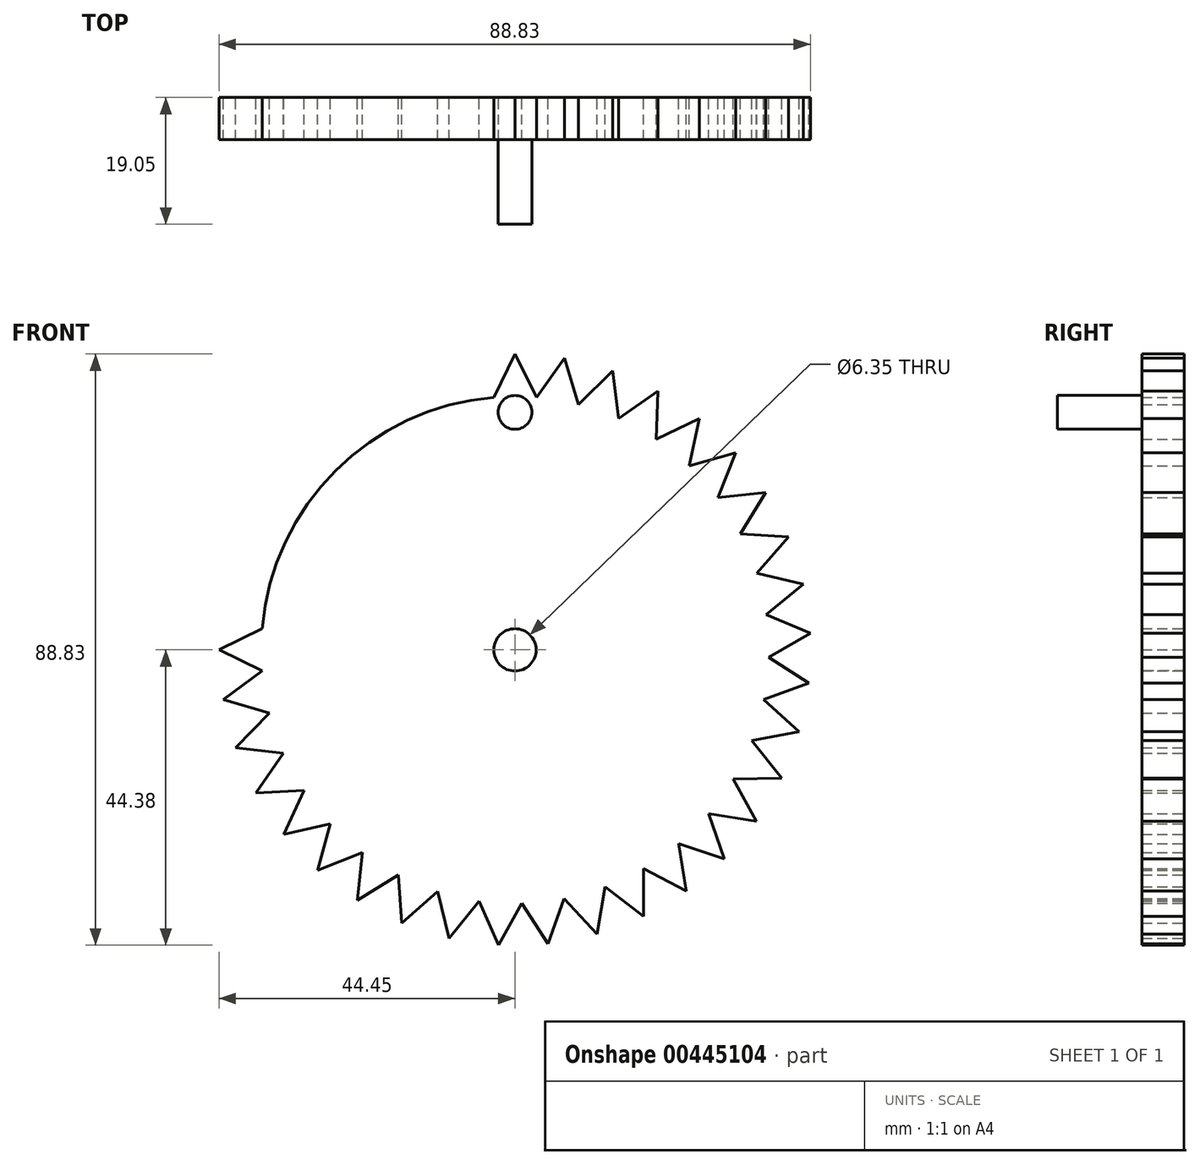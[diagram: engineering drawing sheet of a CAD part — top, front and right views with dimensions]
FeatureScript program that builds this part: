
annotation { "Feature Type Name" : "Feature", "Feature Type Description" : "" }
export const myFeature = defineFeature(function(context is Context, id is Id, definition is map)
    precondition{}
    {
        {
            var Q0;
            Q0=qCreatedBy(makeId("Front.planeOp"),FACE);
            var sketch = newSketch(context, id + "F0", { "sketchPlane" : qUnion([Q0])});
            skCircle(sketch, "E0", {"center": v(0, 0) * mm, "radius": 38.1 * mm});
            skPoint(sketch, "E1", {"position": v(0, 38.1) * mm});
            skPoint(sketch, "E2.1.0", {"position": v(6.38, 37.56) * mm});
            skPoint(sketch, "E2.2.0", {"position": v(12.58, 35.96) * mm});
            skPoint(sketch, "E2.3.0", {"position": v(18.43, 33.35) * mm});
            skPoint(sketch, "E2.4.0", {"position": v(23.75, 29.79) * mm});
            skPoint(sketch, "E2.5.0", {"position": v(28.4, 25.39) * mm});
            skPoint(sketch, "E2.6.0", {"position": v(32.26, 20.27) * mm});
            skPoint(sketch, "E2.7.0", {"position": v(35.2, 14.58) * mm});
            skPoint(sketch, "E2.8.0", {"position": v(37.14, 8.48) * mm});
            skPoint(sketch, "E2.9.0", {"position": v(38.04, 2.14) * mm});
            skPoint(sketch, "E2.10.0", {"position": v(37.86, -4.27) * mm});
            skPoint(sketch, "E2.11.0", {"position": v(36.61, -10.55) * mm});
            skPoint(sketch, "E2.12.0", {"position": v(34.33, -16.53) * mm});
            skPoint(sketch, "E2.13.0", {"position": v(31.07, -22.05) * mm});
            skPoint(sketch, "E2.14.0", {"position": v(26.94, -26.94) * mm});
            skPoint(sketch, "E2.15.0", {"position": v(22.05, -31.07) * mm});
            skPoint(sketch, "E2.16.0", {"position": v(16.53, -34.33) * mm});
            skPoint(sketch, "E2.17.0", {"position": v(10.55, -36.61) * mm});
            skPoint(sketch, "E2.18.0", {"position": v(4.27, -37.86) * mm});
            skPoint(sketch, "E2.19.0", {"position": v(-2.14, -38.04) * mm});
            skPoint(sketch, "E2.20.0", {"position": v(-8.48, -37.14) * mm});
            skPoint(sketch, "E2.21.0", {"position": v(-14.58, -35.2) * mm});
            skPoint(sketch, "E2.22.0", {"position": v(-20.27, -32.26) * mm});
            skPoint(sketch, "E2.23.0", {"position": v(-25.39, -28.4) * mm});
            skPoint(sketch, "E2.24.0", {"position": v(-29.79, -23.75) * mm});
            skPoint(sketch, "E2.25.0", {"position": v(-33.35, -18.43) * mm});
            skPoint(sketch, "E2.26.0", {"position": v(-35.96, -12.58) * mm});
            skPoint(sketch, "E2.27.0", {"position": v(-37.56, -6.38) * mm});
            skLineSegment(sketch, "E2.anchor1", {"start": v(0, 0) * mm, "end": v(0, 38.1) * mm, "construction": true});
            skLineSegment(sketch, "E2.anchor2", {"start": v(0, 0) * mm, "end": v(-38.1, 0) * mm, "construction": true});
            skPoint(sketch, "E3.0.28.0", {"position": v(-38.1, 0) * mm});
            skPoint(sketch, "E4", {"position": v(-3.17, 37.97) * mm});
            skPoint(sketch, "E5.1.0", {"position": v(3.23, 37.96) * mm});
            skPoint(sketch, "E5.2.0", {"position": v(9.55, 36.88) * mm});
            skPoint(sketch, "E5.3.0", {"position": v(15.59, 34.76) * mm});
            skPoint(sketch, "E5.4.0", {"position": v(21.2, 31.66) * mm});
            skPoint(sketch, "E5.5.0", {"position": v(26.2, 27.67) * mm});
            skPoint(sketch, "E5.6.0", {"position": v(30.46, 22.89) * mm});
            skPoint(sketch, "E5.7.0", {"position": v(33.86, 17.46) * mm});
            skPoint(sketch, "E5.8.0", {"position": v(36.3, 11.54) * mm});
            skPoint(sketch, "E5.9.0", {"position": v(37.73, 5.3) * mm});
            skPoint(sketch, "E5.10.0", {"position": v(38.08, -1.1) * mm});
            skPoint(sketch, "E5.11.0", {"position": v(37.36, -7.46) * mm});
            skPoint(sketch, "E5.12.0", {"position": v(35.58, -13.62) * mm});
            skPoint(sketch, "E5.13.0", {"position": v(32.8, -19.38) * mm});
            skPoint(sketch, "E5.14.0", {"position": v(29.1, -24.6) * mm});
            skPoint(sketch, "E5.15.0", {"position": v(24.56, -29.13) * mm});
            skPoint(sketch, "E5.16.0", {"position": v(19.33, -32.83) * mm});
            skPoint(sketch, "E5.17.0", {"position": v(13.56, -35.6) * mm});
            skPoint(sketch, "E5.18.0", {"position": v(7.4, -37.37) * mm});
            skPoint(sketch, "E5.19.0", {"position": v(1.04, -38.09) * mm});
            skPoint(sketch, "E5.20.0", {"position": v(-5.36, -37.72) * mm});
            skPoint(sketch, "E5.21.0", {"position": v(-11.6, -36.3) * mm});
            skPoint(sketch, "E5.22.0", {"position": v(-17.51, -33.84) * mm});
            skPoint(sketch, "E5.23.0", {"position": v(-22.93, -30.42) * mm});
            skPoint(sketch, "E5.24.0", {"position": v(-27.7, -26.15) * mm});
            skPoint(sketch, "E5.25.0", {"position": v(-31.7, -21.14) * mm});
            skPoint(sketch, "E5.26.0", {"position": v(-34.79, -15.53) * mm});
            skPoint(sketch, "E5.27.0", {"position": v(-36.9, -9.49) * mm});
            skPoint(sketch, "E5.28.0", {"position": v(-37.97, -3.17) * mm});
            skLineSegment(sketch, "E5.anchor1", {"start": v(0, 0) * mm, "end": v(-3.17, 37.97) * mm, "construction": true});
            skLineSegment(sketch, "E5.anchor2", {"start": v(0, 0) * mm, "end": v(-37.97, -3.17) * mm, "construction": true});
            skLineSegment(sketch, "E6", {"start": v(6.38, 37.56) * mm, "end": v(0, 0) * mm});
            skLineSegment(sketch, "E7", {"start": v(12.58, 35.96) * mm, "end": v(0, 0) * mm});
            skLineSegment(sketch, "E8", {"start": v(18.43, 33.35) * mm, "end": v(0, 0) * mm});
            skLineSegment(sketch, "E9", {"start": v(23.75, 29.79) * mm, "end": v(0, 0) * mm});
            skLineSegment(sketch, "E10", {"start": v(28.4, 25.39) * mm, "end": v(0, 0) * mm});
            skLineSegment(sketch, "E11", {"start": v(32.26, 20.27) * mm, "end": v(0, 0) * mm});
            skLineSegment(sketch, "E12", {"start": v(35.2, 14.58) * mm, "end": v(0, 0) * mm});
            skLineSegment(sketch, "E13", {"start": v(37.14, 8.48) * mm, "end": v(0, 0) * mm});
            skLineSegment(sketch, "E14", {"start": v(38.04, 2.14) * mm, "end": v(0, 0) * mm});
            skLineSegment(sketch, "E15", {"start": v(37.86, -4.27) * mm, "end": v(0, 0) * mm});
            skLineSegment(sketch, "E16", {"start": v(36.61, -10.55) * mm, "end": v(0, 0) * mm});
            skLineSegment(sketch, "E17", {"start": v(34.33, -16.53) * mm, "end": v(0, 0) * mm});
            skLineSegment(sketch, "E18", {"start": v(31.07, -22.05) * mm, "end": v(0, 0) * mm});
            skLineSegment(sketch, "E19", {"start": v(26.94, -26.94) * mm, "end": v(0, 0) * mm});
            skLineSegment(sketch, "E20", {"start": v(22.05, -31.07) * mm, "end": v(0, 0) * mm});
            skLineSegment(sketch, "E21", {"start": v(16.53, -34.33) * mm, "end": v(0, 0) * mm});
            skLineSegment(sketch, "E22", {"start": v(10.55, -36.61) * mm, "end": v(0, 0) * mm});
            skLineSegment(sketch, "E23", {"start": v(4.27, -37.86) * mm, "end": v(0, 0) * mm});
            skLineSegment(sketch, "E24", {"start": v(-2.14, -38.04) * mm, "end": v(0, 0) * mm});
            skLineSegment(sketch, "E25", {"start": v(-8.48, -37.14) * mm, "end": v(0, 0) * mm});
            skLineSegment(sketch, "E26", {"start": v(-14.58, -35.2) * mm, "end": v(0, 0) * mm});
            skLineSegment(sketch, "E27", {"start": v(-20.27, -32.26) * mm, "end": v(0, 0) * mm});
            skLineSegment(sketch, "E28", {"start": v(-25.39, -28.4) * mm, "end": v(0, 0) * mm});
            skLineSegment(sketch, "E29", {"start": v(-29.79, -23.75) * mm, "end": v(0, 0) * mm});
            skLineSegment(sketch, "E30", {"start": v(-33.35, -18.43) * mm, "end": v(0, 0) * mm});
            skLineSegment(sketch, "E31", {"start": v(-35.96, -12.58) * mm, "end": v(0, 0) * mm});
            skLineSegment(sketch, "E32", {"start": v(-37.56, -6.38) * mm, "end": v(0, 0) * mm});
            skLineSegment(sketch, "E33", {"start": v(0, 38.1) * mm, "end": v(0, 44.45) * mm});
            skLineSegment(sketch, "E34", {"start": v(6.38, 37.56) * mm, "end": v(7.45, 43.82) * mm});
            skLineSegment(sketch, "E35", {"start": v(12.58, 35.96) * mm, "end": v(14.68, 41.96) * mm});
            skLineSegment(sketch, "E36", {"start": v(18.43, 33.35) * mm, "end": v(21.5, 38.9) * mm});
            skLineSegment(sketch, "E37", {"start": v(23.75, 29.79) * mm, "end": v(27.71, 34.75) * mm});
            skLineSegment(sketch, "E38", {"start": v(28.4, 25.39) * mm, "end": v(33.14, 29.62) * mm});
            skLineSegment(sketch, "E39", {"start": v(32.26, 20.27) * mm, "end": v(37.64, 23.65) * mm});
            skLineSegment(sketch, "E40", {"start": v(35.2, 14.58) * mm, "end": v(41.07, 17.01) * mm});
            skLineSegment(sketch, "E41", {"start": v(37.14, 8.48) * mm, "end": v(43.34, 9.9) * mm});
            skLineSegment(sketch, "E42", {"start": v(38.04, 2.14) * mm, "end": v(44.38, 2.5) * mm});
            skLineSegment(sketch, "E43", {"start": v(37.86, -4.27) * mm, "end": v(44.17, -4.98) * mm});
            skLineSegment(sketch, "E44", {"start": v(36.61, -10.55) * mm, "end": v(42.71, -12.3) * mm});
            skLineSegment(sketch, "E45", {"start": v(34.33, -16.53) * mm, "end": v(40.05, -19.29) * mm});
            skLineSegment(sketch, "E46", {"start": v(31.07, -22.05) * mm, "end": v(36.25, -25.72) * mm});
            skLineSegment(sketch, "E47", {"start": v(26.94, -26.94) * mm, "end": v(31.43, -31.43) * mm});
            skLineSegment(sketch, "E48", {"start": v(22.05, -31.07) * mm, "end": v(25.72, -36.25) * mm});
            skLineSegment(sketch, "E49", {"start": v(16.53, -34.33) * mm, "end": v(19.29, -40.05) * mm});
            skLineSegment(sketch, "E50", {"start": v(10.55, -36.61) * mm, "end": v(12.3, -42.71) * mm});
            skLineSegment(sketch, "E51", {"start": v(4.27, -37.86) * mm, "end": v(4.98, -44.17) * mm});
            skLineSegment(sketch, "E52", {"start": v(-8.48, -37.14) * mm, "end": v(-9.9, -43.34) * mm});
            skLineSegment(sketch, "E53", {"start": v(-14.58, -35.2) * mm, "end": v(-17.01, -41.07) * mm});
            skLineSegment(sketch, "E54", {"start": v(-20.27, -32.26) * mm, "end": v(-23.65, -37.64) * mm});
            skLineSegment(sketch, "E55", {"start": v(-25.39, -28.4) * mm, "end": v(-29.62, -33.14) * mm});
            skLineSegment(sketch, "E56", {"start": v(-29.79, -23.75) * mm, "end": v(-34.75, -27.71) * mm});
            skLineSegment(sketch, "E57", {"start": v(-33.35, -18.43) * mm, "end": v(-38.9, -21.5) * mm});
            skLineSegment(sketch, "E58", {"start": v(-35.96, -12.58) * mm, "end": v(-41.96, -14.68) * mm});
            skLineSegment(sketch, "E59", {"start": v(-37.56, -6.38) * mm, "end": v(-43.82, -7.45) * mm});
            skLineSegment(sketch, "E60", {"start": v(-38.1, 0) * mm, "end": v(-44.45, 0) * mm});
            skLineSegment(sketch, "E61", {"start": v(-2.14, -38.04) * mm, "end": v(-2.5, -44.38) * mm});
            skLineSegment(sketch, "E62", {"start": v(0, 44.45) * mm, "end": v(-3.17, 37.97) * mm});
            skLineSegment(sketch, "E63", {"start": v(0, 44.45) * mm, "end": v(3.23, 37.96) * mm});
            skLineSegment(sketch, "E64", {"start": v(3.23, 37.96) * mm, "end": v(7.45, 43.82) * mm});
            skLineSegment(sketch, "E65", {"start": v(7.45, 43.82) * mm, "end": v(9.55, 36.88) * mm});
            skLineSegment(sketch, "E66", {"start": v(9.55, 36.88) * mm, "end": v(14.68, 41.96) * mm});
            skLineSegment(sketch, "E67", {"start": v(14.68, 41.96) * mm, "end": v(15.59, 34.76) * mm});
            skLineSegment(sketch, "E68", {"start": v(15.59, 34.76) * mm, "end": v(21.5, 38.9) * mm});
            skLineSegment(sketch, "E69", {"start": v(21.5, 38.9) * mm, "end": v(21.2, 31.66) * mm});
            skLineSegment(sketch, "E70", {"start": v(27.71, 34.75) * mm, "end": v(21.2, 31.66) * mm});
            skLineSegment(sketch, "E71", {"start": v(27.71, 34.75) * mm, "end": v(26.2, 27.67) * mm});
            skLineSegment(sketch, "E72", {"start": v(26.2, 27.67) * mm, "end": v(33.14, 29.62) * mm});
            skLineSegment(sketch, "E73", {"start": v(33.14, 29.62) * mm, "end": v(30.46, 22.89) * mm});
            skLineSegment(sketch, "E74", {"start": v(30.46, 22.89) * mm, "end": v(37.64, 23.65) * mm});
            skLineSegment(sketch, "E75", {"start": v(37.64, 23.65) * mm, "end": v(33.86, 17.46) * mm});
            skLineSegment(sketch, "E76", {"start": v(33.86, 17.46) * mm, "end": v(41.07, 17.01) * mm});
            skLineSegment(sketch, "E77", {"start": v(41.07, 17.01) * mm, "end": v(36.3, 11.54) * mm});
            skLineSegment(sketch, "E78", {"start": v(36.3, 11.54) * mm, "end": v(43.34, 9.9) * mm});
            skLineSegment(sketch, "E79", {"start": v(43.34, 9.9) * mm, "end": v(37.73, 5.3) * mm});
            skLineSegment(sketch, "E80", {"start": v(37.73, 5.3) * mm, "end": v(44.38, 2.5) * mm});
            skLineSegment(sketch, "E81", {"start": v(44.38, 2.5) * mm, "end": v(38.08, -1.1) * mm});
            skLineSegment(sketch, "E82", {"start": v(38.08, -1.1) * mm, "end": v(44.17, -4.98) * mm});
            skLineSegment(sketch, "E83", {"start": v(44.17, -4.98) * mm, "end": v(37.36, -7.46) * mm});
            skLineSegment(sketch, "E84", {"start": v(37.36, -7.46) * mm, "end": v(42.71, -12.3) * mm});
            skLineSegment(sketch, "E85", {"start": v(42.71, -12.3) * mm, "end": v(35.58, -13.62) * mm});
            skLineSegment(sketch, "E86", {"start": v(35.58, -13.62) * mm, "end": v(40.05, -19.29) * mm});
            skLineSegment(sketch, "E87", {"start": v(40.05, -19.29) * mm, "end": v(32.8, -19.38) * mm});
            skLineSegment(sketch, "E88", {"start": v(32.8, -19.38) * mm, "end": v(36.25, -25.72) * mm});
            skLineSegment(sketch, "E89", {"start": v(36.25, -25.72) * mm, "end": v(29.1, -24.6) * mm});
            skLineSegment(sketch, "E90", {"start": v(29.1, -24.6) * mm, "end": v(31.43, -31.43) * mm});
            skLineSegment(sketch, "E91", {"start": v(31.43, -31.43) * mm, "end": v(24.56, -29.13) * mm});
            skLineSegment(sketch, "E92", {"start": v(24.56, -29.13) * mm, "end": v(25.72, -36.25) * mm});
            skLineSegment(sketch, "E93", {"start": v(25.72, -36.25) * mm, "end": v(19.33, -32.83) * mm});
            skLineSegment(sketch, "E94", {"start": v(19.33, -32.83) * mm, "end": v(19.29, -40.05) * mm});
            skLineSegment(sketch, "E95", {"start": v(19.29, -40.05) * mm, "end": v(13.56, -35.6) * mm});
            skLineSegment(sketch, "E96", {"start": v(13.56, -35.6) * mm, "end": v(12.3, -42.71) * mm});
            skLineSegment(sketch, "E97", {"start": v(12.3, -42.71) * mm, "end": v(7.4, -37.37) * mm});
            skLineSegment(sketch, "E98", {"start": v(7.4, -37.37) * mm, "end": v(4.98, -44.17) * mm});
            skLineSegment(sketch, "E99", {"start": v(4.98, -44.17) * mm, "end": v(1.04, -38.09) * mm});
            skLineSegment(sketch, "E100", {"start": v(1.04, -38.09) * mm, "end": v(-2.5, -44.38) * mm});
            skLineSegment(sketch, "E101", {"start": v(-2.5, -44.38) * mm, "end": v(-5.36, -37.72) * mm});
            skLineSegment(sketch, "E102", {"start": v(-5.36, -37.72) * mm, "end": v(-9.9, -43.34) * mm});
            skLineSegment(sketch, "E103", {"start": v(-9.9, -43.34) * mm, "end": v(-11.6, -36.3) * mm});
            skLineSegment(sketch, "E104", {"start": v(-11.6, -36.3) * mm, "end": v(-17.01, -41.07) * mm});
            skLineSegment(sketch, "E105", {"start": v(-17.01, -41.07) * mm, "end": v(-17.51, -33.84) * mm});
            skLineSegment(sketch, "E106", {"start": v(-17.51, -33.84) * mm, "end": v(-23.65, -37.64) * mm});
            skLineSegment(sketch, "E107", {"start": v(-23.65, -37.64) * mm, "end": v(-22.93, -30.42) * mm});
            skLineSegment(sketch, "E108", {"start": v(-22.93, -30.42) * mm, "end": v(-29.62, -33.14) * mm});
            skLineSegment(sketch, "E109", {"start": v(-29.62, -33.14) * mm, "end": v(-27.7, -26.15) * mm});
            skLineSegment(sketch, "E110", {"start": v(-27.7, -26.15) * mm, "end": v(-34.75, -27.71) * mm});
            skLineSegment(sketch, "E111", {"start": v(-34.75, -27.71) * mm, "end": v(-31.7, -21.14) * mm});
            skLineSegment(sketch, "E112", {"start": v(-31.7, -21.14) * mm, "end": v(-38.9, -21.5) * mm});
            skLineSegment(sketch, "E113", {"start": v(-34.79, -15.53) * mm, "end": v(-38.9, -21.5) * mm});
            skLineSegment(sketch, "E114", {"start": v(-41.96, -14.68) * mm, "end": v(-34.79, -15.53) * mm});
            skLineSegment(sketch, "E115", {"start": v(-36.9, -9.49) * mm, "end": v(-41.96, -14.68) * mm});
            skLineSegment(sketch, "E116", {"start": v(-36.9, -9.49) * mm, "end": v(-43.82, -7.45) * mm});
            skLineSegment(sketch, "E117", {"start": v(-43.82, -7.45) * mm, "end": v(-37.97, -3.17) * mm});
            skLineSegment(sketch, "E118", {"start": v(-37.97, -3.17) * mm, "end": v(-44.45, 0) * mm});
            skPoint(sketch, "E119", {"position": v(-37.97, 3.17) * mm});
            skLineSegment(sketch, "E120", {"start": v(-44.45, 0) * mm, "end": v(-37.97, 3.17) * mm});
            skSolve(sketch);
        }
        {
            var Q0;
            Q0 = qSketchRegion(id + "F0", true);
            extrude(context, id + "F1", {"entities" : qUnion([Q0]), "depth" : 6.35 * mm});
        }
        {
            var Q0;
            Q0=makeQuery(id+"F1.opExtrude","CAP_FACE",FACE,{"disambiguationData":[OSD([sQuery(id+"F0.wireOp",EDGE,"E0"),sQuery(id+"F0.wireOp",EDGE,"E62"),sQuery(id+"F0.wireOp",EDGE,"E63"),sQuery(id+"F0.wireOp",EDGE,"E64"),sQuery(id+"F0.wireOp",EDGE,"E65"),sQuery(id+"F0.wireOp",EDGE,"E66"),sQuery(id+"F0.wireOp",EDGE,"E67"),sQuery(id+"F0.wireOp",EDGE,"E68"),sQuery(id+"F0.wireOp",EDGE,"E69"),sQuery(id+"F0.wireOp",EDGE,"E70"),sQuery(id+"F0.wireOp",EDGE,"E71"),sQuery(id+"F0.wireOp",EDGE,"E72"),sQuery(id+"F0.wireOp",EDGE,"E73"),sQuery(id+"F0.wireOp",EDGE,"E74"),sQuery(id+"F0.wireOp",EDGE,"E75"),sQuery(id+"F0.wireOp",EDGE,"E76"),sQuery(id+"F0.wireOp",EDGE,"E77"),sQuery(id+"F0.wireOp",EDGE,"E78"),sQuery(id+"F0.wireOp",EDGE,"E79"),sQuery(id+"F0.wireOp",EDGE,"E80"),sQuery(id+"F0.wireOp",EDGE,"E81"),sQuery(id+"F0.wireOp",EDGE,"E82"),sQuery(id+"F0.wireOp",EDGE,"E83"),sQuery(id+"F0.wireOp",EDGE,"E84"),sQuery(id+"F0.wireOp",EDGE,"E85"),sQuery(id+"F0.wireOp",EDGE,"E86"),sQuery(id+"F0.wireOp",EDGE,"E87"),sQuery(id+"F0.wireOp",EDGE,"E88"),sQuery(id+"F0.wireOp",EDGE,"E89"),sQuery(id+"F0.wireOp",EDGE,"E90"),sQuery(id+"F0.wireOp",EDGE,"E91"),sQuery(id+"F0.wireOp",EDGE,"E92"),sQuery(id+"F0.wireOp",EDGE,"E93"),sQuery(id+"F0.wireOp",EDGE,"E94"),sQuery(id+"F0.wireOp",EDGE,"E95"),sQuery(id+"F0.wireOp",EDGE,"E96"),sQuery(id+"F0.wireOp",EDGE,"E97"),sQuery(id+"F0.wireOp",EDGE,"E98"),sQuery(id+"F0.wireOp",EDGE,"E99"),sQuery(id+"F0.wireOp",EDGE,"E100"),sQuery(id+"F0.wireOp",EDGE,"E101"),sQuery(id+"F0.wireOp",EDGE,"E102"),sQuery(id+"F0.wireOp",EDGE,"E103"),sQuery(id+"F0.wireOp",EDGE,"E104"),sQuery(id+"F0.wireOp",EDGE,"E105"),sQuery(id+"F0.wireOp",EDGE,"E106"),sQuery(id+"F0.wireOp",EDGE,"E107"),sQuery(id+"F0.wireOp",EDGE,"E108"),sQuery(id+"F0.wireOp",EDGE,"E109"),sQuery(id+"F0.wireOp",EDGE,"E110"),sQuery(id+"F0.wireOp",EDGE,"E111"),sQuery(id+"F0.wireOp",EDGE,"E112"),sQuery(id+"F0.wireOp",EDGE,"E113"),sQuery(id+"F0.wireOp",EDGE,"E114"),sQuery(id+"F0.wireOp",EDGE,"E115"),sQuery(id+"F0.wireOp",EDGE,"E116"),sQuery(id+"F0.wireOp",EDGE,"E117"),sQuery(id+"F0.wireOp",EDGE,"E118"),sQuery(id+"F0.wireOp",EDGE,"E120")])],"isStart":false});
            var sketch = newSketch(context, id + "F2", { "sketchPlane" : qUnion([Q0])});
            skCircle(sketch, "E121", {"center": v(0, 0) * mm, "radius": 3.18 * mm});
            skSolve(sketch);
        }
        {
            var Q0;
            Q0=makeQuery(id+"F2.imprint","IMPRINT",FACE,{"disambiguationData":[TD([[makeQuery(id+"F2.imprint","IMPRINT",EDGE,{"derivedFrom":sQuery(id+"F2.wireOp",EDGE,"E121")}),1.0]])]});
            extrude(context, id + "F3", {"entities" : qUnion([Q0]), "operationType" : NewBodyOperationType.REMOVE, "oppositeDirection" : true, "depth" : 25.4 * mm});
        }
        {
            var Q0;
            Q0=makeQuery(id+"F1.opExtrude","CAP_FACE",FACE,{"disambiguationData":[OSD([sQuery(id+"F0.wireOp",EDGE,"E0"),sQuery(id+"F0.wireOp",EDGE,"E62"),sQuery(id+"F0.wireOp",EDGE,"E63"),sQuery(id+"F0.wireOp",EDGE,"E64"),sQuery(id+"F0.wireOp",EDGE,"E65"),sQuery(id+"F0.wireOp",EDGE,"E66"),sQuery(id+"F0.wireOp",EDGE,"E67"),sQuery(id+"F0.wireOp",EDGE,"E68"),sQuery(id+"F0.wireOp",EDGE,"E69"),sQuery(id+"F0.wireOp",EDGE,"E70"),sQuery(id+"F0.wireOp",EDGE,"E71"),sQuery(id+"F0.wireOp",EDGE,"E72"),sQuery(id+"F0.wireOp",EDGE,"E73"),sQuery(id+"F0.wireOp",EDGE,"E74"),sQuery(id+"F0.wireOp",EDGE,"E75"),sQuery(id+"F0.wireOp",EDGE,"E76"),sQuery(id+"F0.wireOp",EDGE,"E77"),sQuery(id+"F0.wireOp",EDGE,"E78"),sQuery(id+"F0.wireOp",EDGE,"E79"),sQuery(id+"F0.wireOp",EDGE,"E80"),sQuery(id+"F0.wireOp",EDGE,"E81"),sQuery(id+"F0.wireOp",EDGE,"E82"),sQuery(id+"F0.wireOp",EDGE,"E83"),sQuery(id+"F0.wireOp",EDGE,"E84"),sQuery(id+"F0.wireOp",EDGE,"E85"),sQuery(id+"F0.wireOp",EDGE,"E86"),sQuery(id+"F0.wireOp",EDGE,"E87"),sQuery(id+"F0.wireOp",EDGE,"E88"),sQuery(id+"F0.wireOp",EDGE,"E89"),sQuery(id+"F0.wireOp",EDGE,"E90"),sQuery(id+"F0.wireOp",EDGE,"E91"),sQuery(id+"F0.wireOp",EDGE,"E92"),sQuery(id+"F0.wireOp",EDGE,"E93"),sQuery(id+"F0.wireOp",EDGE,"E94"),sQuery(id+"F0.wireOp",EDGE,"E95"),sQuery(id+"F0.wireOp",EDGE,"E96"),sQuery(id+"F0.wireOp",EDGE,"E97"),sQuery(id+"F0.wireOp",EDGE,"E98"),sQuery(id+"F0.wireOp",EDGE,"E99"),sQuery(id+"F0.wireOp",EDGE,"E100"),sQuery(id+"F0.wireOp",EDGE,"E101"),sQuery(id+"F0.wireOp",EDGE,"E102"),sQuery(id+"F0.wireOp",EDGE,"E103"),sQuery(id+"F0.wireOp",EDGE,"E104"),sQuery(id+"F0.wireOp",EDGE,"E105"),sQuery(id+"F0.wireOp",EDGE,"E106"),sQuery(id+"F0.wireOp",EDGE,"E107"),sQuery(id+"F0.wireOp",EDGE,"E108"),sQuery(id+"F0.wireOp",EDGE,"E109"),sQuery(id+"F0.wireOp",EDGE,"E110"),sQuery(id+"F0.wireOp",EDGE,"E111"),sQuery(id+"F0.wireOp",EDGE,"E112"),sQuery(id+"F0.wireOp",EDGE,"E113"),sQuery(id+"F0.wireOp",EDGE,"E114"),sQuery(id+"F0.wireOp",EDGE,"E115"),sQuery(id+"F0.wireOp",EDGE,"E116"),sQuery(id+"F0.wireOp",EDGE,"E117"),sQuery(id+"F0.wireOp",EDGE,"E118"),sQuery(id+"F0.wireOp",EDGE,"E120")])],"isStart":false});
            var sketch = newSketch(context, id + "F4", { "sketchPlane" : qUnion([Q0])});
            skPoint(sketch, "E122", {"position": v(0, 35.7) * mm});
            skCircle(sketch, "E123", {"center": v(0, 35.7) * mm, "radius": 2.54 * mm});
            skSolve(sketch);
        }
        {
            var Q0;
            Q0=makeQuery(id+"F4.imprint","IMPRINT",FACE,{"disambiguationData":[TD([[makeQuery(id+"F4.imprint","IMPRINT",EDGE,{"derivedFrom":sQuery(id+"F4.wireOp",EDGE,"E123")}),1.0]])]});
            extrude(context, id + "F5", {"entities" : qUnion([Q0]), "operationType" : NewBodyOperationType.ADD, "depth" : 12.7 * mm});
        }
    });
